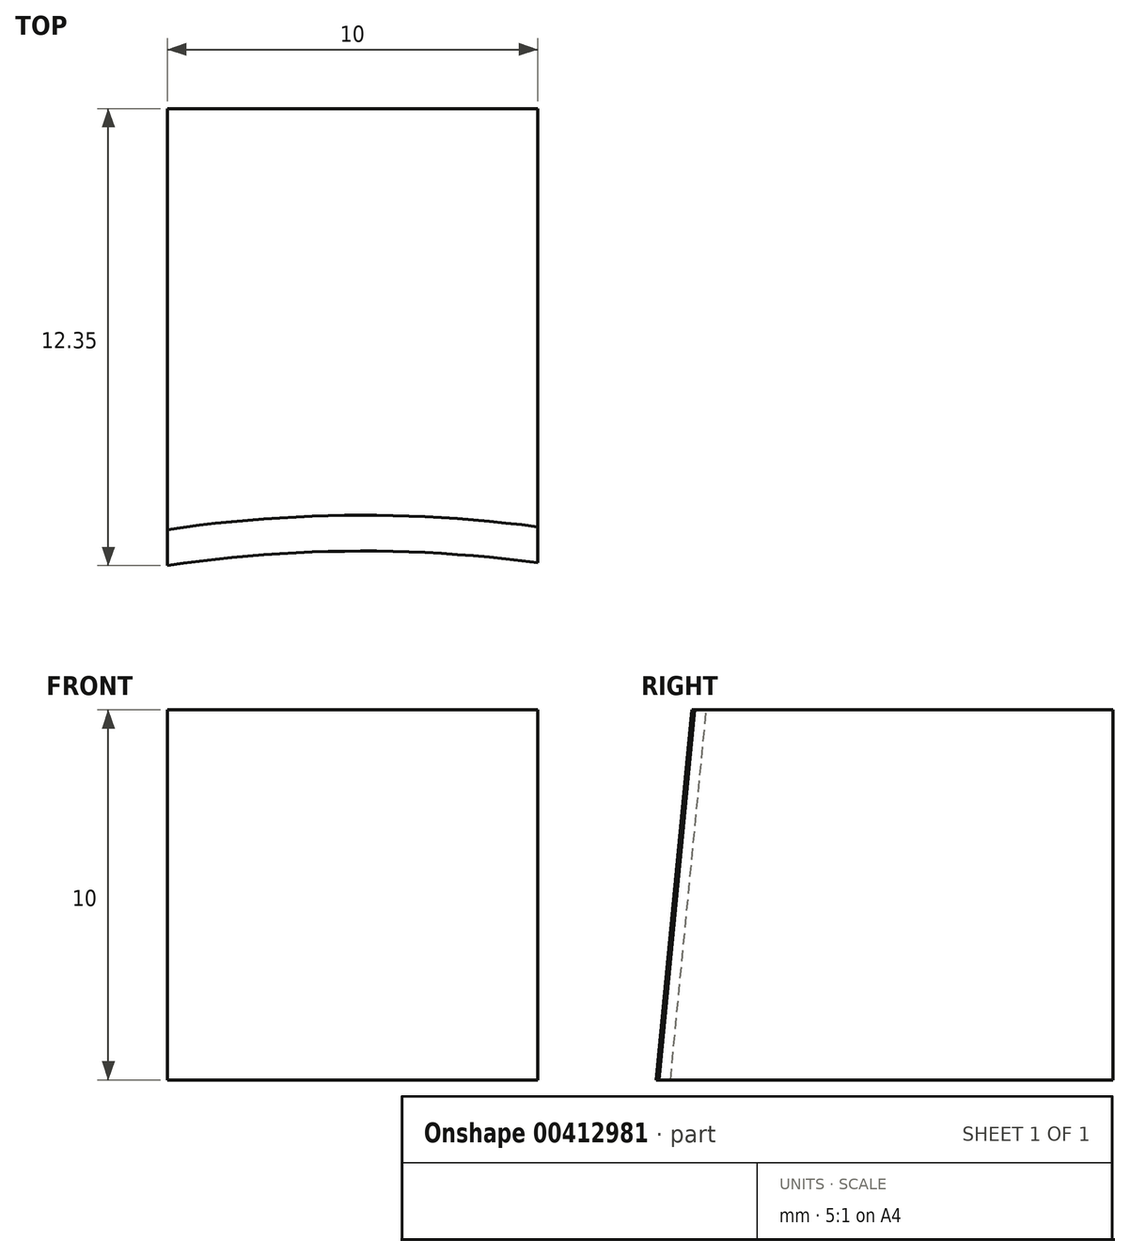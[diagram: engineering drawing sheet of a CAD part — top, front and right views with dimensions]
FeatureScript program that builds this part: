
annotation { "Feature Type Name" : "Feature", "Feature Type Description" : "" }
export const myFeature = defineFeature(function(context is Context, id is Id, definition is map)
    precondition{}
    {
        {
            var Q0;
            Q0=qCreatedBy(makeId("Right.planeOp"),FACE);
            var sketch = newSketch(context, id + "F0", { "sketchPlane" : qUnion([Q0])});
            skLineSegment(sketch, "E0.bottom", {"start": v(6.5, 5) * mm, "end": v(-6.5, 5) * mm});
            skLineSegment(sketch, "E0.top", {"start": v(6.5, -5) * mm, "end": v(-6.5, -5) * mm});
            skLineSegment(sketch, "E0.left", {"start": v(6.5, 5) * mm, "end": v(6.5, -5) * mm});
            skLineSegment(sketch, "E0.right", {"start": v(-6.5, 5) * mm, "end": v(-6.5, -5) * mm});
            skPoint(sketch, "E0.middle", {"position": v(0, 0) * mm});
            skSolve(sketch);
        }
        {
            var Q0;
            Q0 = qSketchRegion(id + "F0", true);
            extrude(context, id + "F1", {"entities" : qUnion([Q0]), "depth" : 10 * mm});
        }
        {
            var Q0;
            Q0=makeQuery(id+"F1.opExtrude","SWEPT_EDGE",EDGE,{"disambiguationData":[OSD([sQuery(id+"F0.wireOp",EDGE,"E0.bottom"),sQuery(id+"F0.wireOp",EDGE,"E0.right")])]});
            cPlane(context, id + "F2", {"entities" : qUnion([Q0]), "cplaneType" : CPlaneType.LINE_ANGLE, "offset" : 25 * mm, "angle" : 95.53 * degree, "width" : 150 * mm, "height" : 150 * mm});
        }
        {
            var Q0;
            Q0=qCreatedBy(id+"F2.planeOp",FACE);
            var sketch = newSketch(context, id + "F3", { "sketchPlane" : qUnion([Q0])});
            skCircle(sketch, "E1", {"center": v(5.27, -40.95) * mm, "radius": 36 * mm});
            skSolve(sketch);
        }
        {
            var Q0;
            Q0 = qSketchRegion(id + "F3", true);
            extrude(context, id + "F4", {"entities" : qUnion([Q0]), "operationType" : NewBodyOperationType.REMOVE, "endBound" : BoundingType.SYMMETRIC, "oppositeDirection" : true, "depth" : 25 * mm});
        }
    });
